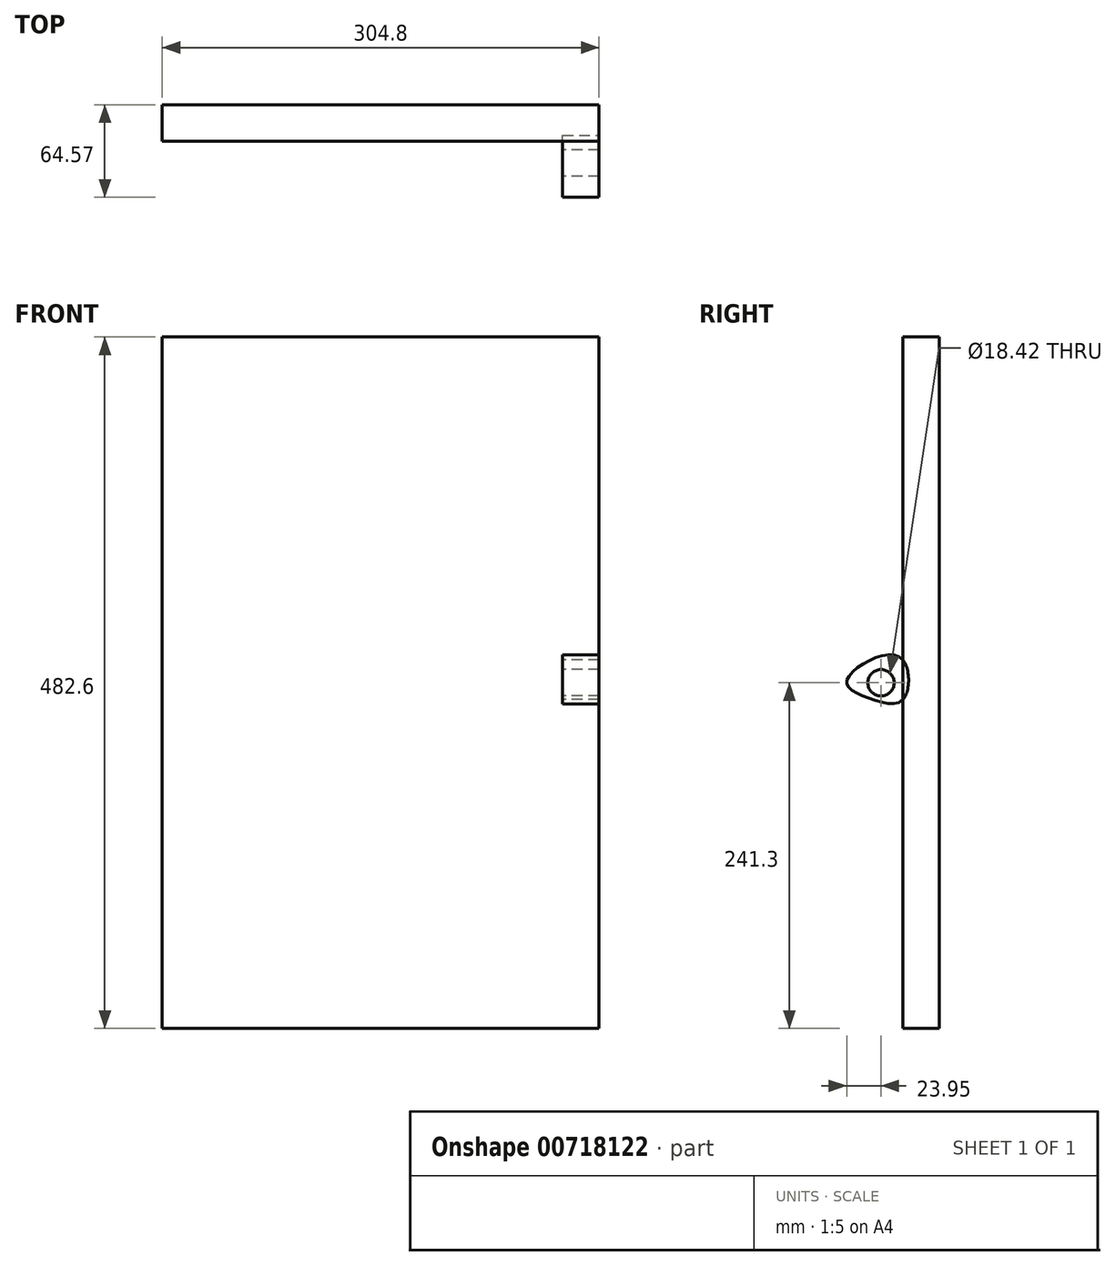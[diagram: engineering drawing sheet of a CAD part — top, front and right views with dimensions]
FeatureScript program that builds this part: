
annotation { "Feature Type Name" : "Feature", "Feature Type Description" : "" }
export const myFeature = defineFeature(function(context is Context, id is Id, definition is map)
    precondition{}
    {
        {
            var Q0;
            Q0=qCreatedBy(makeId("Front.planeOp"),FACE);
            var sketch = newSketch(context, id + "F0", { "sketchPlane" : qUnion([Q0])});
            skLineSegment(sketch, "E0.bottom", {"start": v(-139.7, 241.3) * mm, "end": v(139.7, 241.3) * mm});
            skLineSegment(sketch, "E0.top", {"start": v(-139.7, -241.3) * mm, "end": v(139.7, -241.3) * mm});
            skLineSegment(sketch, "E0.left", {"start": v(-139.7, 241.3) * mm, "end": v(-139.7, -241.3) * mm});
            skLineSegment(sketch, "E0.right", {"start": v(139.7, 241.3) * mm, "end": v(139.7, -241.3) * mm});
            skPoint(sketch, "E0.middle", {"position": v(0, 0) * mm});
            skSolve(sketch);
        }
        {
            var Q0;
            Q0 = qSketchRegion(id + "F0", true);
            extrude(context, id + "F1", {"entities" : qUnion([Q0]), "depth" : 25.4 * mm, "offsetDistance" : 25.4 * mm});
        }
        {
            var Q0;
            Q0=makeQuery(id+"F1.opExtrude","SWEPT_FACE",FACE,{"disambiguationData":[OSD([sQuery(id+"F0.wireOp",EDGE,"E0.right")])]});
            var sketch = newSketch(context, id + "F2", { "sketchPlane" : qUnion([Q0])});
            skPoint(sketch, "E1.2.internal.snap0", {"position": v(-25.4, 0) * mm});
            skFitSpline(sketch, "E1", {"points": [v(-25.4, 15.89) * mm, v(-47.99, 15.89) * mm, v(-64.56, 0) * mm, v(-48.9, -10.81) * mm, v(-25.4, -11.73) * mm, v(-25.4, 15.89) * mm]});
            skCircle(sketch, "E2", {"center": v(-40.62, 0) * mm, "radius": 9.21 * mm});
            skSolve(sketch);
        }
        {
            var Q0;
            Q0=makeQuery(id+"F2.imprint","IMPRINT",FACE,{"disambiguationData":[TD([[makeQuery(id+"F2.imprint","IMPRINT",EDGE,{"derivedFrom":sQuery(id+"F2.wireOp",EDGE,"E2")}),-1.0]])]});
            var Q1;
            {var subQ0=sQuery(id+"F0.wireOp",EDGE,"E0.right");Q1=makeQuery(id+"F2.imprint","IMPRINT",FACE,{"disambiguationData":[TD([[makeQuery(id+"F2.imprint","IMPRINT",EDGE,{"derivedFrom":makeQuery(id+"F1.opExtrude","CAP_EDGE",EDGE,{"disambiguationData":[OSD([subQ0])],"isStart":true})}),-1.0]])]});}
            extrude(context, id + "F3", {"entities" : qUnion([Q0, Q1]), "operationType" : NewBodyOperationType.ADD, "depth" : 25.4 * mm, "offsetDistance" : 25.4 * mm});
        }
    });
